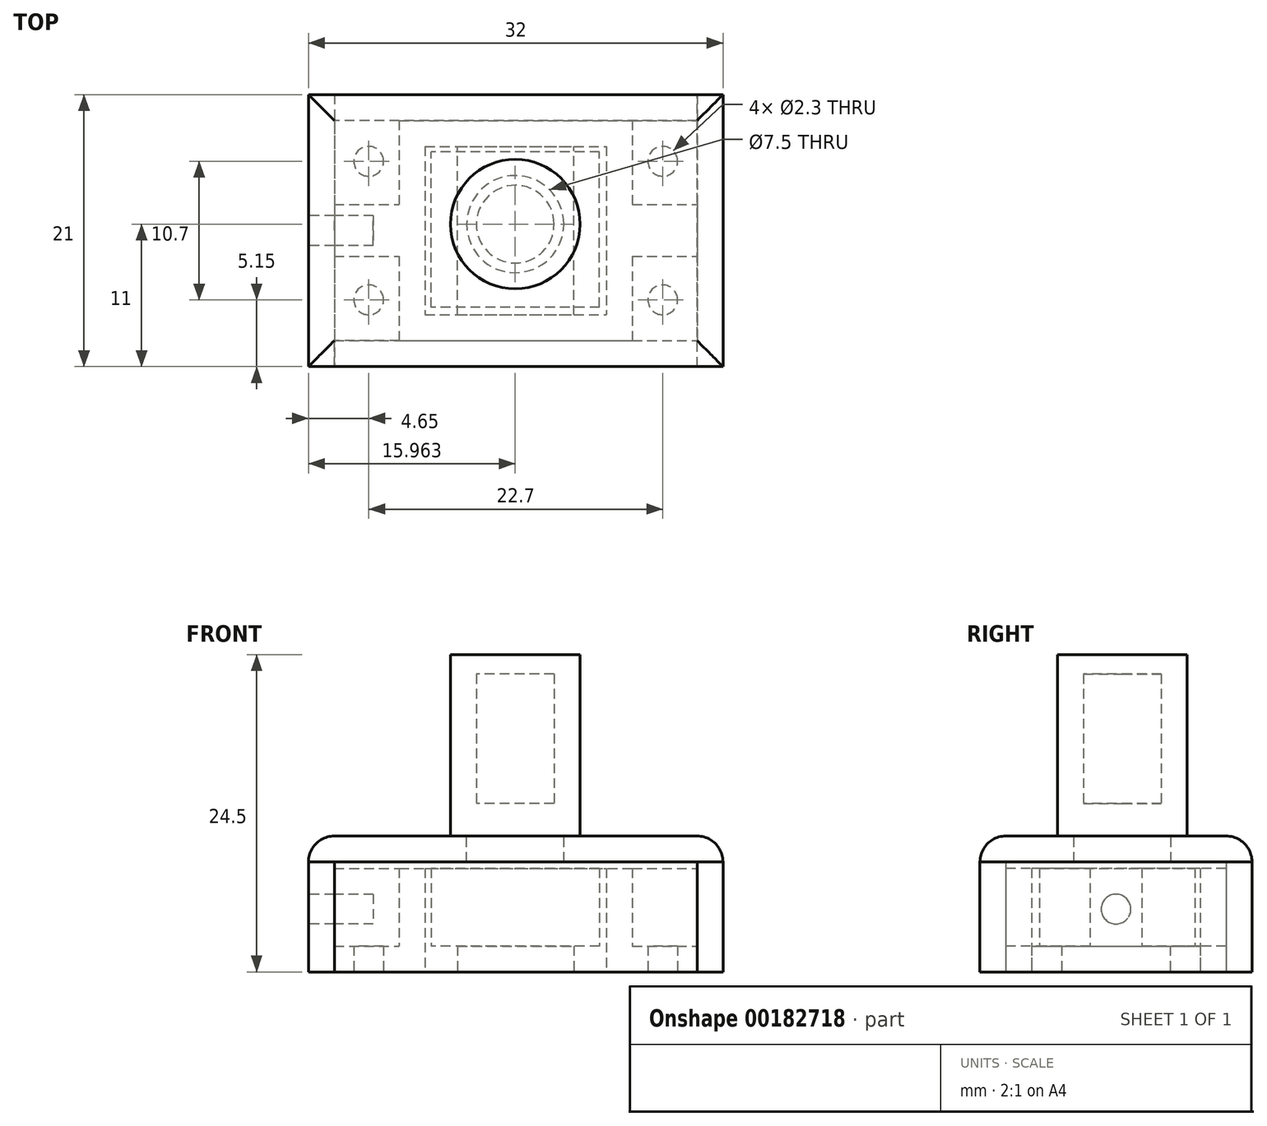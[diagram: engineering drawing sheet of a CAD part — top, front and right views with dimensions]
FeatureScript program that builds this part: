
annotation { "Feature Type Name" : "Feature", "Feature Type Description" : "" }
export const myFeature = defineFeature(function(context is Context, id is Id, definition is map)
    precondition{}
    {
        {
            var Q0;
            Q0=qCreatedBy(makeId("Top.planeOp"),FACE);
            var sketch = newSketch(context, id + "F0", { "sketchPlane" : qUnion([Q0])});
            skLineSegment(sketch, "E0.bottom", {"start": v(-2, 2) * mm, "end": v(16, 2) * mm});
            skLineSegment(sketch, "E0.top", {"start": v(-2, -15) * mm, "end": v(16, -15) * mm});
            skLineSegment(sketch, "E0.left", {"start": v(-2, 2) * mm, "end": v(-2, -15) * mm});
            skLineSegment(sketch, "E0.right", {"start": v(16, 2) * mm, "end": v(16, -15) * mm});
            skLineSegment(sketch, "E1.bottom", {"start": v(0, 0) * mm, "end": v(14, 0) * mm});
            skLineSegment(sketch, "E1.top", {"start": v(0, -13) * mm, "end": v(14, -13) * mm});
            skLineSegment(sketch, "E1.left", {"start": v(0, 0) * mm, "end": v(0, -13) * mm});
            skLineSegment(sketch, "E1.right", {"start": v(14, 0) * mm, "end": v(14, -13) * mm});
            skSolve(sketch);
        }
        {
            var Q0;
            Q0 = qSketchRegion(id + "F0", true);
            extrude(context, id + "F1", {"entities" : qUnion([Q0]), "depth" : 8 * mm});
        }
        {
            var Q0;
            Q0=makeQuery(id+"F1.opExtrude","CAP_FACE",FACE,{"disambiguationData":[OSD([sQuery(id+"F0.wireOp",EDGE,"E0.bottom"),sQuery(id+"F0.wireOp",EDGE,"E0.top"),sQuery(id+"F0.wireOp",EDGE,"E0.left"),sQuery(id+"F0.wireOp",EDGE,"E0.right"),sQuery(id+"F0.wireOp",EDGE,"E1.bottom"),sQuery(id+"F0.wireOp",EDGE,"E1.top"),sQuery(id+"F0.wireOp",EDGE,"E1.left"),sQuery(id+"F0.wireOp",EDGE,"E1.right")])],"isStart":true});
            var sketch = newSketch(context, id + "F2", { "sketchPlane" : qUnion([Q0])});
            skLineSegment(sketch, "E2.bottom", {"start": v(2.5, 13) * mm, "end": v(11.5, 13) * mm});
            skLineSegment(sketch, "E2.top", {"start": v(2.5, 0) * mm, "end": v(11.5, 0) * mm});
            skLineSegment(sketch, "E2.left", {"start": v(2.5, 13) * mm, "end": v(2.5, 0) * mm});
            skLineSegment(sketch, "E2.right", {"start": v(11.5, 13) * mm, "end": v(11.5, 0) * mm});
            skSolve(sketch);
        }
        {
            var Q0;
            Q0 = qSketchRegion(id + "F2", true);
            extrude(context, id + "F3", {"entities" : qUnion([Q0]), "operationType" : NewBodyOperationType.ADD, "oppositeDirection" : true, "depth" : 2 * mm});
        }
        {
            var Q0;
            Q0=makeQuery(id+"F3.opExtrude","CAP_FACE",FACE,{"disambiguationData":[OSD([sQuery(id+"F2.wireOp",EDGE,"E2.bottom"),sQuery(id+"F2.wireOp",EDGE,"E2.top"),sQuery(id+"F2.wireOp",EDGE,"E2.left"),sQuery(id+"F2.wireOp",EDGE,"E2.right")])],"isStart":false});
            var sketch = newSketch(context, id + "F4", { "sketchPlane" : qUnion([Q0])});
            skSolve(sketch);
        }
        {
            var Q0;
            Q0=makeQuery(id+"F4.imprint","IMPRINT",FACE,{"disambiguationData":[TD([[makeQuery(id+"F4.imprint","IMPRINT",EDGE,{"derivedFrom":makeQuery(id+"F3.opExtrude","CAP_EDGE",EDGE,{"disambiguationData":[OSD([sQuery(id+"F2.wireOp",EDGE,"E2.left")])],"isStart":false})}),-1.0]])]});
            var sketch = newSketch(context, id + "F5", { "sketchPlane" : qUnion([Q0])});
            skLineSegment(sketch, "E3.bottom", {"start": v(13.46, -12.41) * mm, "end": v(0.46, -12.41) * mm});
            skLineSegment(sketch, "E3.top", {"start": v(13.46, -0.41) * mm, "end": v(0.46, -0.41) * mm});
            skLineSegment(sketch, "E3.left", {"start": v(13.46, -12.41) * mm, "end": v(13.46, -0.41) * mm});
            skLineSegment(sketch, "E3.right", {"start": v(0.46, -12.41) * mm, "end": v(0.46, -0.41) * mm});
            skPoint(sketch, "E3.middle", {"position": v(6.96, -6.41) * mm});
            skSolve(sketch);
        }
        {
            var Q0;
            Q0 = qSketchRegion(id + "F5", true);
            extrude(context, id + "F6", {"entities" : qUnion([Q0]), "depth" : 6 * mm});
        }
        {
            var Q0;
            Q0=makeQuery(id+"F6.opExtrude","CAP_FACE",FACE,{"disambiguationData":[OSD([sQuery(id+"F5.wireOp",EDGE,"E3.bottom"),sQuery(id+"F5.wireOp",EDGE,"E3.top"),sQuery(id+"F5.wireOp",EDGE,"E3.left"),sQuery(id+"F5.wireOp",EDGE,"E3.right")])],"isStart":false});
            var sketch = newSketch(context, id + "F7", { "sketchPlane" : qUnion([Q0])});
            skCircle(sketch, "E4", {"center": v(6.96, -6) * mm, "radius": 3.5 * mm});
            skSolve(sketch);
        }
        {
            var Q0;
            Q0 = qSketchRegion(id + "F7", true);
            extrude(context, id + "F8", {"entities" : qUnion([Q0]), "depth" : 5 * mm});
        }
        {
            var Q0;
            Q0=makeQuery(id+"F8.opExtrude","CAP_FACE",FACE,{"disambiguationData":[OSD([sQuery(id+"F7.wireOp",EDGE,"E4")])],"isStart":false});
            var sketch = newSketch(context, id + "F9", { "sketchPlane" : qUnion([Q0])});
            skCircle(sketch, "E5", {"center": v(6.96, -6) * mm, "radius": 3 * mm});
            skSolve(sketch);
        }
        {
            var Q0;
            Q0 = qSketchRegion(id + "F9", true);
            extrude(context, id + "F10", {"entities" : qUnion([Q0]), "depth" : 10 * mm});
        }
        {
            var Q0;
            Q0=qCreatedBy(makeId("Top.planeOp"),FACE);
            var sketch = newSketch(context, id + "F11", { "sketchPlane" : qUnion([Q0])});
            skLineSegment(sketch, "E6.bottom", {"start": v(-2, 2) * mm, "end": v(-7, 2) * mm});
            skLineSegment(sketch, "E6.top", {"start": v(-2, -15) * mm, "end": v(-7, -15) * mm});
            skLineSegment(sketch, "E6.left", {"start": v(-2, 2) * mm, "end": v(-2, -15) * mm});
            skLineSegment(sketch, "E6.right", {"start": v(-7, 2) * mm, "end": v(-7, -15) * mm});
            skCircle(sketch, "E7", {"center": v(-4.35, -11.85) * mm, "radius": 1.15 * mm});
            skCircle(sketch, "E8", {"center": v(-4.35, -1.15) * mm, "radius": 1.15 * mm});
            skLineSegment(sketch, "E9.bottom", {"start": v(16, 2) * mm, "end": v(21, 2) * mm});
            skLineSegment(sketch, "E9.top", {"start": v(16, -15) * mm, "end": v(21, -15) * mm});
            skLineSegment(sketch, "E9.left", {"start": v(16, 2) * mm, "end": v(16, -15) * mm});
            skLineSegment(sketch, "E9.right", {"start": v(21, 2) * mm, "end": v(21, -15) * mm});
            skCircle(sketch, "E10", {"center": v(18.35, -1.15) * mm, "radius": 1.15 * mm});
            skCircle(sketch, "E11", {"center": v(18.35, -11.85) * mm, "radius": 1.15 * mm});
            skSolve(sketch);
        }
        {
            var Q0;
            Q0 = qSketchRegion(id + "F11", true);
            extrude(context, id + "F12", {"entities" : qUnion([Q0]), "operationType" : NewBodyOperationType.ADD, "depth" : 2 * mm});
        }
        {
            var Q0;
            Q0=makeQuery(id+"F12.opExtrude","CAP_FACE",FACE,{"disambiguationData":[OSD([sQuery(id+"F11.wireOp",EDGE,"E6.bottom"),sQuery(id+"F11.wireOp",EDGE,"E6.top"),sQuery(id+"F11.wireOp",EDGE,"E6.left"),sQuery(id+"F11.wireOp",EDGE,"E6.right"),sQuery(id+"F11.wireOp",EDGE,"E7"),sQuery(id+"F11.wireOp",EDGE,"E8")])],"isStart":false});
            var sketch = newSketch(context, id + "F13", { "sketchPlane" : qUnion([Q0])});
            skLineSegment(sketch, "E12.bottom", {"start": v(-7, -4.5) * mm, "end": v(-2, -4.5) * mm});
            skLineSegment(sketch, "E12.top", {"start": v(-7, -8.5) * mm, "end": v(-2, -8.5) * mm});
            skLineSegment(sketch, "E12.left", {"start": v(-7, -4.5) * mm, "end": v(-7, -8.5) * mm});
            skLineSegment(sketch, "E12.right", {"start": v(-2, -4.5) * mm, "end": v(-2, -8.5) * mm});
            skLineSegment(sketch, "E13.bottom", {"start": v(16, -4.5) * mm, "end": v(21, -4.5) * mm});
            skLineSegment(sketch, "E13.top", {"start": v(16, -8.5) * mm, "end": v(21, -8.5) * mm});
            skLineSegment(sketch, "E13.left", {"start": v(16, -4.5) * mm, "end": v(16, -8.5) * mm});
            skLineSegment(sketch, "E13.right", {"start": v(21, -4.5) * mm, "end": v(21, -8.5) * mm});
            skSolve(sketch);
        }
        {
            var Q0;
            Q0 = qSketchRegion(id + "F13", true);
            extrude(context, id + "F14", {"entities" : qUnion([Q0]), "operationType" : NewBodyOperationType.ADD, "depth" : 6 * mm});
        }
        {
            var Q0;
            Q0=makeQuery(id+"F12.boolean.opBoolean","MERGE",FACE,{"derivedFrom":[makeQuery(id+"F1.opExtrude","SWEPT_FACE",FACE,{"disambiguationData":[OSD([sQuery(id+"F0.wireOp",EDGE,"E0.top")])]}),makeQuery(id+"F12.opExtrude","SWEPT_FACE",FACE,{"disambiguationData":[OSD([sQuery(id+"F11.wireOp",EDGE,"E6.top")])]}),makeQuery(id+"F12.opExtrude","SWEPT_FACE",FACE,{"disambiguationData":[OSD([sQuery(id+"F11.wireOp",EDGE,"E9.top")])]})]});
            var sketch = newSketch(context, id + "F15", { "sketchPlane" : qUnion([Q0])});
            skLineSegment(sketch, "E14.bottom", {"start": v(-7, 0) * mm, "end": v(21, 0) * mm});
            skLineSegment(sketch, "E14.top", {"start": v(-7, 8.5) * mm, "end": v(21, 8.5) * mm});
            skLineSegment(sketch, "E14.left", {"start": v(-7, 0) * mm, "end": v(-7, 8.5) * mm});
            skLineSegment(sketch, "E14.right", {"start": v(21, 0) * mm, "end": v(21, 8.5) * mm});
            skSolve(sketch);
        }
        {
            var Q0;
            Q0 = qSketchRegion(id + "F15", true);
            extrude(context, id + "F16", {"entities" : qUnion([Q0]), "depth" : 2 * mm});
        }
        {
            var Q0;
            Q0=makeQuery(id+"F14.opExtrude","SWEPT_FACE",FACE,{"disambiguationData":[OSD([sQuery(id+"F13.wireOp",EDGE,"E13.right")])]});
            var sketch = newSketch(context, id + "F17", { "sketchPlane" : qUnion([Q0])});
            skLineSegment(sketch, "E15.bottom", {"start": v(-17, 0) * mm, "end": v(4, 0) * mm});
            skLineSegment(sketch, "E15.top", {"start": v(-17, 8.5) * mm, "end": v(4, 8.5) * mm});
            skLineSegment(sketch, "E15.left", {"start": v(-17, 0) * mm, "end": v(-17, 8.5) * mm});
            skLineSegment(sketch, "E15.right", {"start": v(4, 0) * mm, "end": v(4, 8.5) * mm});
            skSolve(sketch);
        }
        {
            var Q0;
            Q0 = qSketchRegion(id + "F17", true);
            extrude(context, id + "F18", {"entities" : qUnion([Q0]), "depth" : 2 * mm});
        }
        {
            var Q0;
            Q0=makeQuery(id+"F12.boolean.opBoolean","MERGE",FACE,{"derivedFrom":[makeQuery(id+"F1.opExtrude","SWEPT_FACE",FACE,{"disambiguationData":[OSD([sQuery(id+"F0.wireOp",EDGE,"E0.bottom")])]}),makeQuery(id+"F12.opExtrude","SWEPT_FACE",FACE,{"disambiguationData":[OSD([sQuery(id+"F11.wireOp",EDGE,"E6.bottom")])]}),makeQuery(id+"F12.opExtrude","SWEPT_FACE",FACE,{"disambiguationData":[OSD([sQuery(id+"F11.wireOp",EDGE,"E9.bottom")])]})]});
            var sketch = newSketch(context, id + "F19", { "sketchPlane" : qUnion([Q0])});
            skLineSegment(sketch, "E16.bottom", {"start": v(-21, 0) * mm, "end": v(7, 0) * mm});
            skLineSegment(sketch, "E16.top", {"start": v(-21, 8.5) * mm, "end": v(7, 8.5) * mm});
            skLineSegment(sketch, "E16.left", {"start": v(-21, 0) * mm, "end": v(-21, 8.5) * mm});
            skLineSegment(sketch, "E16.right", {"start": v(7, 0) * mm, "end": v(7, 8.5) * mm});
            skSolve(sketch);
        }
        {
            var Q0;
            Q0 = qSketchRegion(id + "F19", true);
            extrude(context, id + "F20", {"entities" : qUnion([Q0]), "depth" : 2 * mm});
        }
        {
            var Q0;
            Q0=makeQuery(id+"F14.boolean.opBoolean","MERGE",FACE,{"derivedFrom":[makeQuery(id+"F12.opExtrude","SWEPT_FACE",FACE,{"disambiguationData":[OSD([sQuery(id+"F11.wireOp",EDGE,"E6.right")])]}),makeQuery(id+"F14.opExtrude","SWEPT_FACE",FACE,{"disambiguationData":[OSD([sQuery(id+"F13.wireOp",EDGE,"E12.left")])]})]});
            var sketch = newSketch(context, id + "F21", { "sketchPlane" : qUnion([Q0])});
            skLineSegment(sketch, "E17.bottom", {"start": v(-4, 0) * mm, "end": v(17, 0) * mm});
            skLineSegment(sketch, "E17.top", {"start": v(-4, 8.5) * mm, "end": v(17, 8.5) * mm});
            skLineSegment(sketch, "E17.left", {"start": v(-4, 0) * mm, "end": v(-4, 8.5) * mm});
            skLineSegment(sketch, "E17.right", {"start": v(17, 0) * mm, "end": v(17, 8.5) * mm});
            skSolve(sketch);
        }
        {
            var Q0;
            Q0 = qSketchRegion(id + "F21", true);
            extrude(context, id + "F22", {"entities" : qUnion([Q0]), "depth" : 2 * mm});
        }
        {
            var Q0;
            Q0=makeQuery(id+"F22.opExtrude","CAP_FACE",FACE,{"disambiguationData":[OSD([sQuery(id+"F21.wireOp",EDGE,"E17.bottom"),sQuery(id+"F21.wireOp",EDGE,"E17.top"),sQuery(id+"F21.wireOp",EDGE,"E17.left"),sQuery(id+"F21.wireOp",EDGE,"E17.right")])],"isStart":false});
            var sketch = newSketch(context, id + "F23", { "sketchPlane" : qUnion([Q0])});
            skCircle(sketch, "E18", {"center": v(6.5, 4.85) * mm, "radius": 1.15 * mm});
            skSolve(sketch);
        }
        {
            var Q0;
            Q0 = qSketchRegion(id + "F23", true);
            extrude(context, id + "F24", {"entities" : qUnion([Q0]), "operationType" : NewBodyOperationType.REMOVE, "oppositeDirection" : true, "depth" : 5 * mm});
        }
        {
            var Q0;
            Q0=makeQuery(id+"F20.opExtrude","SWEPT_FACE",FACE,{"disambiguationData":[OSD([sQuery(id+"F19.wireOp",EDGE,"E16.top")])]});
            var sketch = newSketch(context, id + "F25", { "sketchPlane" : qUnion([Q0])});
            skLineSegment(sketch, "E19.bottom", {"start": v(-9, 4) * mm, "end": v(23, 4) * mm});
            skLineSegment(sketch, "E19.top", {"start": v(-9, -17) * mm, "end": v(23, -17) * mm});
            skLineSegment(sketch, "E19.left", {"start": v(-9, 4) * mm, "end": v(-9, -17) * mm});
            skLineSegment(sketch, "E19.right", {"start": v(23, 4) * mm, "end": v(23, -17) * mm});
            skSolve(sketch);
        }
        {
            var Q0;
            Q0 = qSketchRegion(id + "F25", true);
            extrude(context, id + "F26", {"entities" : qUnion([Q0]), "depth" : 2 * mm});
        }
        {
            var Q0;
            Q0=makeQuery(id+"F8.opExtrude","CAP_FACE",FACE,{"disambiguationData":[OSD([sQuery(id+"F7.wireOp",EDGE,"E4")])],"isStart":false});
            var sketch = newSketch(context, id + "F27", { "sketchPlane" : qUnion([Q0])});
            skCircle(sketch, "E20", {"center": v(6.96, -6) * mm, "radius": 3.75 * mm});
            skSolve(sketch);
        }
        {
            var Q0;
            Q0 = qSketchRegion(id + "F27", true);
            extrude(context, id + "F28", {"entities" : qUnion([Q0]), "operationType" : NewBodyOperationType.REMOVE, "oppositeDirection" : true, "depth" : 5 * mm});
        }
        {
            var Q0;
            Q0=makeQuery(id+"F26.opExtrude","CAP_FACE",FACE,{"disambiguationData":[OSD([sQuery(id+"F25.wireOp",EDGE,"E19.bottom"),sQuery(id+"F25.wireOp",EDGE,"E19.top"),sQuery(id+"F25.wireOp",EDGE,"E19.left"),sQuery(id+"F25.wireOp",EDGE,"E19.right")])],"isStart":false});
            var sketch = newSketch(context, id + "F29", { "sketchPlane" : qUnion([Q0])});
            skCircle(sketch, "E21", {"center": v(6.96, -6) * mm, "radius": 5 * mm});
            skSolve(sketch);
        }
        {
            var Q0;
            Q0 = qSketchRegion(id + "F29", true);
            extrude(context, id + "F30", {"entities" : qUnion([Q0]), "depth" : 14 * mm});
        }
        {
            var Q0;
            Q0=makeQuery(id+"F26.opExtrude","CAP_EDGE",EDGE,{"disambiguationData":[OSD([sQuery(id+"F25.wireOp",EDGE,"E19.left")])],"isStart":false});
            var Q1;
            Q1=makeQuery(id+"F26.opExtrude","CAP_EDGE",EDGE,{"disambiguationData":[OSD([sQuery(id+"F25.wireOp",EDGE,"E19.bottom")])],"isStart":false});
            var Q2;
            Q2=makeQuery(id+"F26.opExtrude","CAP_EDGE",EDGE,{"disambiguationData":[OSD([sQuery(id+"F25.wireOp",EDGE,"E19.top")])],"isStart":false});
            var Q3;
            Q3=makeQuery(id+"F26.opExtrude","CAP_EDGE",EDGE,{"disambiguationData":[OSD([sQuery(id+"F25.wireOp",EDGE,"E19.right")])],"isStart":false});
            fillet(context, id + "F31", {"entities" : qUnion([Q0, Q1, Q2, Q3]), "radius" : 2 * mm, "tangentPropagation" : true, "allowEdgeOverflow" : false});
        }
    });
